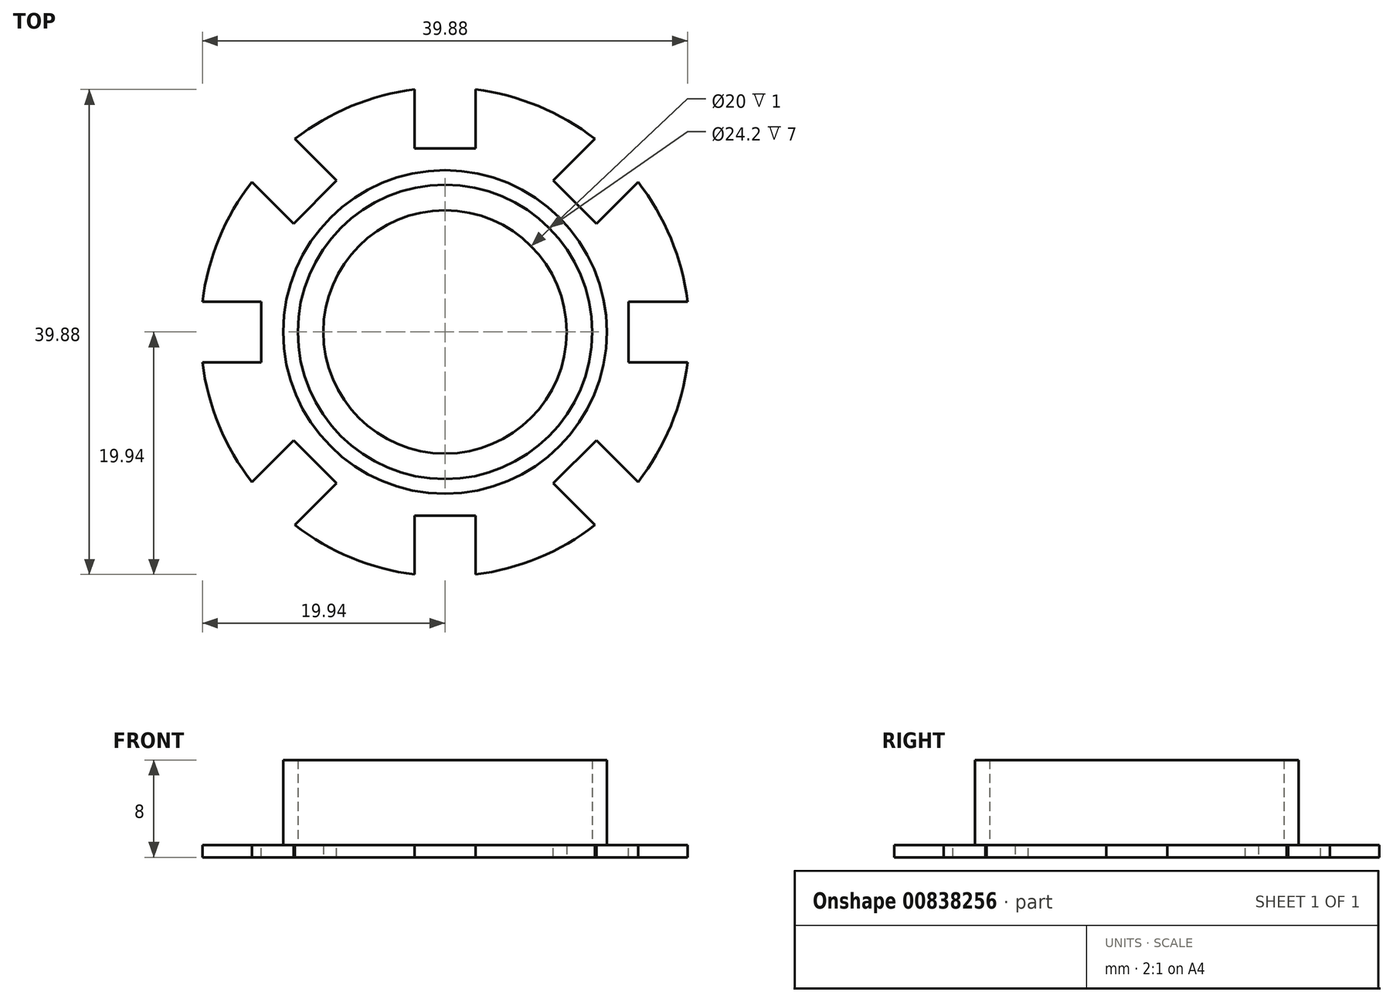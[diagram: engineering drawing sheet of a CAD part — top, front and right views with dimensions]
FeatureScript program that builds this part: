
annotation { "Feature Type Name" : "Feature", "Feature Type Description" : "" }
export const myFeature = defineFeature(function(context is Context, id is Id, definition is map)
    precondition{}
    {
        {
            var Q0;
            Q0=qCreatedBy(makeId("Top.planeOp"),FACE);
            var sketch = newSketch(context, id + "F0", { "sketchPlane" : qUnion([Q0])});
            skCircle(sketch, "E0", {"center": v(0, 0) * mm, "radius": 12.1 * mm});
            skCircle(sketch, "E1.0", {"center": v(0, 0) * mm, "radius": 20.1 * mm});
            skCircle(sketch, "E2", {"center": v(0, 0) * mm, "radius": 10 * mm});
            skCircle(sketch, "E3.0", {"center": v(0, 0) * mm, "radius": 13.3 * mm});
            skSolve(sketch);
        }
        {
            var Q0;
            Q0=makeQuery(id+"F0.imprint","IMPRINT",FACE,{"disambiguationData":[TD([[makeQuery(id+"F0.imprint","IMPRINT",EDGE,{"derivedFrom":sQuery(id+"F0.wireOp",EDGE,"E0")}),-1.0]])]});
            var Q1;
            Q1=makeQuery(id+"F0.imprint","IMPRINT",FACE,{"disambiguationData":[TD([[makeQuery(id+"F0.imprint","IMPRINT",EDGE,{"derivedFrom":sQuery(id+"F0.wireOp",EDGE,"E0")}),1.0]])]});
            var Q2;
            Q2=makeQuery(id+"F0.imprint","IMPRINT",FACE,{"disambiguationData":[TD([[makeQuery(id+"F0.imprint","IMPRINT",EDGE,{"derivedFrom":sQuery(id+"F0.wireOp",EDGE,"E1.0")}),1.0]])]});
            extrude(context, id + "F1", {"entities" : qUnion([Q0, Q1, Q2]), "depth" : 1 * mm, "offsetDistance" : 25 * mm});
        }
        {
            var Q0;
            Q0=makeQuery(id+"F0.imprint","IMPRINT",FACE,{"disambiguationData":[TD([[makeQuery(id+"F0.imprint","IMPRINT",EDGE,{"derivedFrom":sQuery(id+"F0.wireOp",EDGE,"E0")}),-1.0]])]});
            extrude(context, id + "F2", {"entities" : qUnion([Q0]), "operationType" : NewBodyOperationType.ADD, "depth" : 8 * mm, "offsetDistance" : 25 * mm});
        }
        {
            var Q0;
            {var subQ0=sQuery(id+"F0.wireOp",EDGE,"E1.0");Q0=makeQuery(id+"F2.boolean.opBoolean","SPLIT",FACE,{"disambiguationData":[TD([makeQuery(id+"F1.opExtrude","SWEPT_FACE",FACE,{"disambiguationData":[OSD([subQ0])]})])],"derivedFrom":makeQuery(id+"F1.opExtrude","CAP_FACE",FACE,{"disambiguationData":[OSD([subQ0,sQuery(id+"F0.wireOp",EDGE,"E2")])],"isStart":false})});}
            var sketch = newSketch(context, id + "F3", { "sketchPlane" : qUnion([Q0])});
            skLineSegment(sketch, "E4.bottom", {"start": v(2.5, 15.1) * mm, "end": v(-2.5, 15.1) * mm});
            skLineSegment(sketch, "E4.top", {"start": v(2.5, 25.1) * mm, "end": v(-2.5, 25.1) * mm});
            skLineSegment(sketch, "E4.left", {"start": v(2.5, 15.1) * mm, "end": v(2.5, 25.1) * mm});
            skLineSegment(sketch, "E4.right", {"start": v(-2.5, 15.1) * mm, "end": v(-2.5, 25.1) * mm});
            skPoint(sketch, "E4.middle", {"position": v(0, 20.1) * mm});
            skLineSegment(sketch, "E5.1.0", {"start": v(-15.98, 19.52) * mm, "end": v(-19.52, 15.98) * mm});
            skPoint(sketch, "E5.1.1", {"position": v(-14.21, 14.21) * mm});
            skLineSegment(sketch, "E5.1.2", {"start": v(-8.9, 12.45) * mm, "end": v(-12.45, 8.9) * mm});
            skLineSegment(sketch, "E5.1.3", {"start": v(-8.9, 12.45) * mm, "end": v(-15.98, 19.52) * mm});
            skLineSegment(sketch, "E5.1.4", {"start": v(-12.45, 8.9) * mm, "end": v(-19.52, 15.98) * mm});
            skLineSegment(sketch, "E5.2.0", {"start": v(-25.1, 2.5) * mm, "end": v(-25.1, -2.5) * mm});
            skPoint(sketch, "E5.2.1", {"position": v(-20.1, 0) * mm});
            skLineSegment(sketch, "E5.2.2", {"start": v(-15.1, 2.5) * mm, "end": v(-15.1, -2.5) * mm});
            skLineSegment(sketch, "E5.2.3", {"start": v(-15.1, 2.5) * mm, "end": v(-25.1, 2.5) * mm});
            skLineSegment(sketch, "E5.2.4", {"start": v(-15.1, -2.5) * mm, "end": v(-25.1, -2.5) * mm});
            skLineSegment(sketch, "E5.3.0", {"start": v(-19.52, -15.98) * mm, "end": v(-15.98, -19.52) * mm});
            skPoint(sketch, "E5.3.1", {"position": v(-14.21, -14.21) * mm});
            skLineSegment(sketch, "E5.3.2", {"start": v(-12.45, -8.9) * mm, "end": v(-8.9, -12.45) * mm});
            skLineSegment(sketch, "E5.3.3", {"start": v(-12.45, -8.9) * mm, "end": v(-19.52, -15.98) * mm});
            skLineSegment(sketch, "E5.3.4", {"start": v(-8.9, -12.45) * mm, "end": v(-15.98, -19.52) * mm});
            skLineSegment(sketch, "E5.4.0", {"start": v(-2.5, -25.1) * mm, "end": v(2.5, -25.1) * mm});
            skPoint(sketch, "E5.4.1", {"position": v(0, -20.1) * mm});
            skLineSegment(sketch, "E5.4.2", {"start": v(-2.5, -15.1) * mm, "end": v(2.5, -15.1) * mm});
            skLineSegment(sketch, "E5.4.3", {"start": v(-2.5, -15.1) * mm, "end": v(-2.5, -25.1) * mm});
            skLineSegment(sketch, "E5.4.4", {"start": v(2.5, -15.1) * mm, "end": v(2.5, -25.1) * mm});
            skLineSegment(sketch, "E5.5.0", {"start": v(15.98, -19.52) * mm, "end": v(19.52, -15.98) * mm});
            skPoint(sketch, "E5.5.1", {"position": v(14.21, -14.21) * mm});
            skLineSegment(sketch, "E5.5.2", {"start": v(8.9, -12.45) * mm, "end": v(12.45, -8.9) * mm});
            skLineSegment(sketch, "E5.5.3", {"start": v(8.9, -12.45) * mm, "end": v(15.98, -19.52) * mm});
            skLineSegment(sketch, "E5.5.4", {"start": v(12.45, -8.9) * mm, "end": v(19.52, -15.98) * mm});
            skLineSegment(sketch, "E5.6.0", {"start": v(25.1, -2.5) * mm, "end": v(25.1, 2.5) * mm});
            skPoint(sketch, "E5.6.1", {"position": v(20.1, 0) * mm});
            skLineSegment(sketch, "E5.6.2", {"start": v(15.1, -2.5) * mm, "end": v(15.1, 2.5) * mm});
            skLineSegment(sketch, "E5.6.3", {"start": v(15.1, -2.5) * mm, "end": v(25.1, -2.5) * mm});
            skLineSegment(sketch, "E5.6.4", {"start": v(15.1, 2.5) * mm, "end": v(25.1, 2.5) * mm});
            skLineSegment(sketch, "E5.7.0", {"start": v(19.52, 15.98) * mm, "end": v(15.98, 19.52) * mm});
            skPoint(sketch, "E5.7.1", {"position": v(14.21, 14.21) * mm});
            skLineSegment(sketch, "E5.7.2", {"start": v(12.45, 8.9) * mm, "end": v(8.9, 12.45) * mm});
            skLineSegment(sketch, "E5.7.3", {"start": v(12.45, 8.9) * mm, "end": v(19.52, 15.98) * mm});
            skLineSegment(sketch, "E5.7.4", {"start": v(8.9, 12.45) * mm, "end": v(15.98, 19.52) * mm});
            skPoint(sketch, "E5.center", {"position": v(0, 0) * mm});
            skSolve(sketch);
        }
        {
            var Q0;
            Q0 = qSketchRegion(id + "F3", true);
            extrude(context, id + "F4", {"entities" : qUnion([Q0]), "operationType" : NewBodyOperationType.REMOVE, "endBound" : BoundingType.THROUGH_ALL, "oppositeDirection" : true, "depth" : 25 * mm, "offsetDistance" : 25 * mm});
        }
    });
